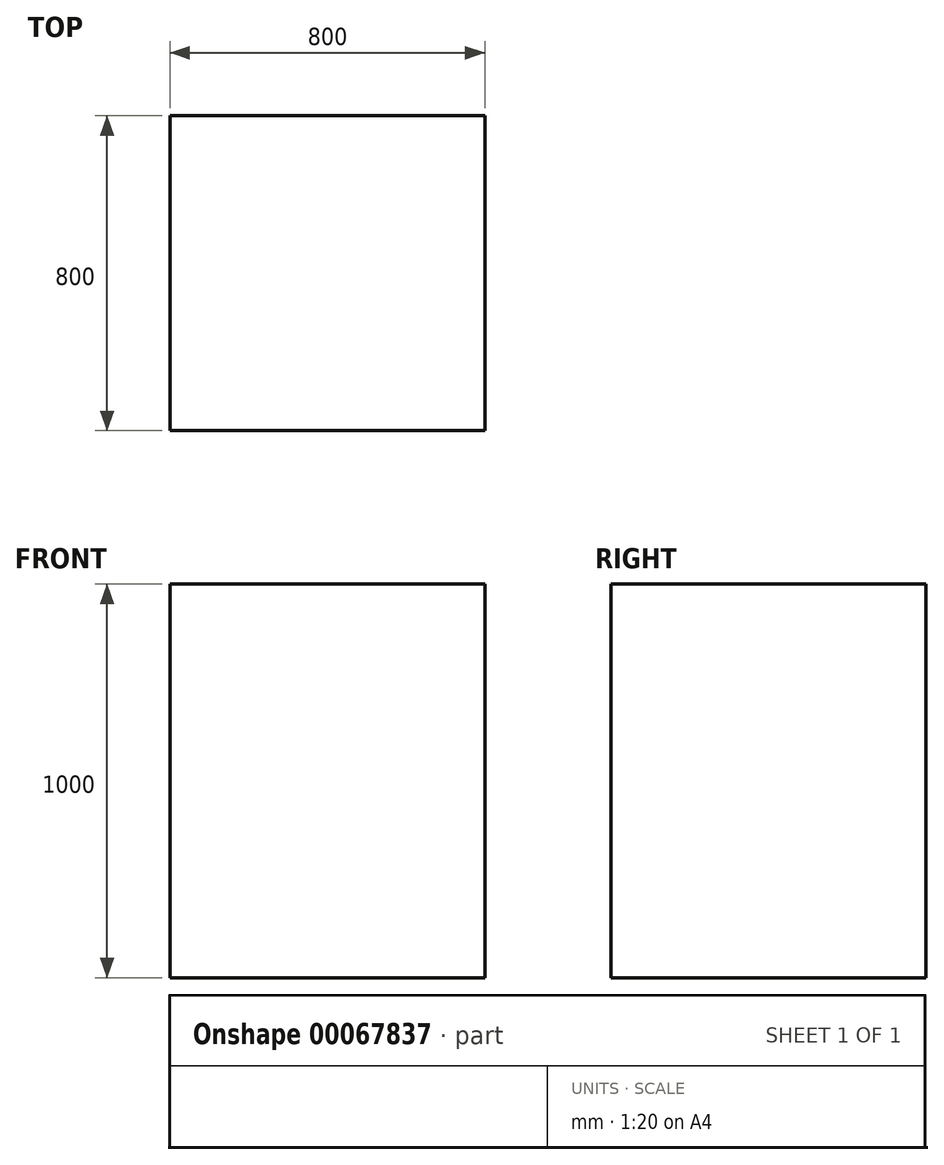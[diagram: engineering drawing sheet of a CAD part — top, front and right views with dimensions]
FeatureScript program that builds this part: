
annotation { "Feature Type Name" : "Feature", "Feature Type Description" : "" }
export const myFeature = defineFeature(function(context is Context, id is Id, definition is map)
    precondition{}
    {
        {
            var Q0;
            Q0=qCreatedBy(makeId("Top.planeOp"),FACE);
            var sketch = newSketch(context, id + "F0", { "sketchPlane" : qUnion([Q0])});
            skLineSegment(sketch, "E0.bottom", {"start": v(-400, -400) * mm, "end": v(400, -400) * mm});
            skLineSegment(sketch, "E0.top", {"start": v(-400, 400) * mm, "end": v(400, 400) * mm});
            skLineSegment(sketch, "E0.left", {"start": v(-400, -400) * mm, "end": v(-400, 400) * mm});
            skLineSegment(sketch, "E0.right", {"start": v(400, -400) * mm, "end": v(400, 400) * mm});
            skLineSegment(sketch, "E1", {"start": v(-400, 400) * mm, "end": v(400, -400) * mm, "construction": true});
            skSolve(sketch);
        }
        {
            var Q0;
            Q0=makeQuery(id+"F0.imprint","IMPRINT",FACE,{"disambiguationData":[TD([[makeQuery(id+"F0.imprint","IMPRINT",EDGE,{"derivedFrom":sQuery(id+"F0.wireOp",EDGE,"E0.bottom")}),1.0]])]});
            extrude(context, id + "F1", {"entities" : qUnion([Q0]), "depth" : 1000 * mm});
        }
    });
